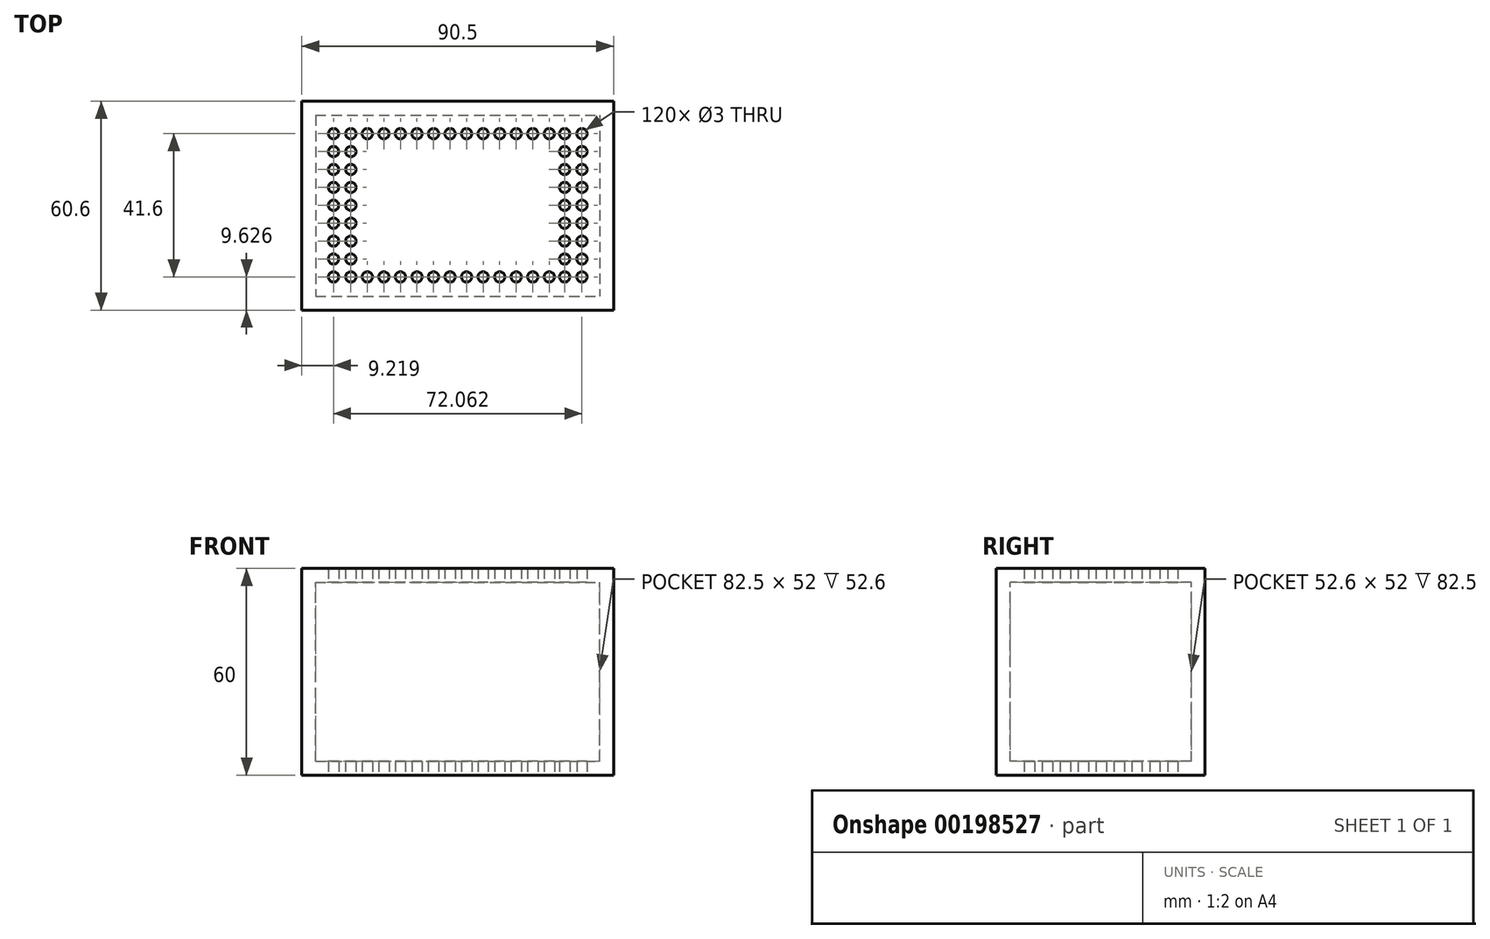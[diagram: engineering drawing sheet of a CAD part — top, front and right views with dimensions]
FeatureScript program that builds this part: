
annotation { "Feature Type Name" : "Feature", "Feature Type Description" : "" }
export const myFeature = defineFeature(function(context is Context, id is Id, definition is map)
    precondition{}
    {
        {
            var Q0;
            Q0=qCreatedBy(makeId("Top.planeOp"),FACE);
            var sketch = newSketch(context, id + "F0", { "sketchPlane" : qUnion([Q0])});
            skLineSegment(sketch, "E0.bottom", {"start": v(-45.25, 30.3) * mm, "end": v(45.25, 30.3) * mm});
            skLineSegment(sketch, "E0.top", {"start": v(-45.25, -30.3) * mm, "end": v(45.25, -30.3) * mm});
            skLineSegment(sketch, "E0.left", {"start": v(-45.25, 30.3) * mm, "end": v(-45.25, -30.3) * mm});
            skLineSegment(sketch, "E0.right", {"start": v(45.25, 30.3) * mm, "end": v(45.25, -30.3) * mm});
            skLineSegment(sketch, "E1", {"start": v(-45.25, -30.3) * mm, "end": v(45.25, 30.3) * mm, "construction": true});
            skLineSegment(sketch, "E2.0", {"start": v(41.25, 26.3) * mm, "end": v(41.25, -26.3) * mm});
            skLineSegment(sketch, "E2.1", {"start": v(-41.25, 26.3) * mm, "end": v(41.25, 26.3) * mm});
            skLineSegment(sketch, "E2.2", {"start": v(-41.25, 26.3) * mm, "end": v(-41.25, -26.3) * mm});
            skLineSegment(sketch, "E2.3", {"start": v(-41.25, -26.3) * mm, "end": v(41.25, -26.3) * mm});
            skCircle(sketch, "E3", {"center": v(-36.03, -20.67) * mm, "radius": 1.5 * mm});
            skLineSegment(sketch, "E4", {"start": v(0, -43.44) * mm, "end": v(0, 37) * mm, "construction": true});
            skPoint(sketch, "E4.endSnap0", {"position": v(0, 30.3) * mm});
            skCircle(sketch, "E5.0.1.0", {"center": v(-36.03, -15.47) * mm, "radius": 1.5 * mm});
            skCircle(sketch, "E5.0.2.0", {"center": v(-36.03, -10.27) * mm, "radius": 1.5 * mm});
            skCircle(sketch, "E5.0.3.0", {"center": v(-36.03, -5.07) * mm, "radius": 1.5 * mm});
            skCircle(sketch, "E5.0.4.0", {"center": v(-36.03, 0.13) * mm, "radius": 1.5 * mm});
            skCircle(sketch, "E5.0.5.0", {"center": v(-36.03, 5.33) * mm, "radius": 1.5 * mm});
            skCircle(sketch, "E5.0.6.0", {"center": v(-36.03, 10.53) * mm, "radius": 1.5 * mm});
            skCircle(sketch, "E5.0.7.0", {"center": v(-36.03, 15.73) * mm, "radius": 1.5 * mm});
            skCircle(sketch, "E5.0.8.0", {"center": v(-36.03, 20.93) * mm, "radius": 1.5 * mm});
            skCircle(sketch, "E5.1.0.0", {"center": v(-31.03, -20.67) * mm, "radius": 1.5 * mm});
            skCircle(sketch, "E5.1.1.0", {"center": v(-31.03, -15.47) * mm, "radius": 1.5 * mm});
            skCircle(sketch, "E5.1.2.0", {"center": v(-31.03, -10.27) * mm, "radius": 1.5 * mm});
            skCircle(sketch, "E5.1.3.0", {"center": v(-31.03, -5.07) * mm, "radius": 1.5 * mm});
            skCircle(sketch, "E5.1.4.0", {"center": v(-31.03, 0.13) * mm, "radius": 1.5 * mm});
            skCircle(sketch, "E5.1.5.0", {"center": v(-31.03, 5.33) * mm, "radius": 1.5 * mm});
            skCircle(sketch, "E5.1.6.0", {"center": v(-31.03, 10.53) * mm, "radius": 1.5 * mm});
            skCircle(sketch, "E5.1.7.0", {"center": v(-31.03, 15.73) * mm, "radius": 1.5 * mm});
            skCircle(sketch, "E5.1.8.0", {"center": v(-31.03, 20.93) * mm, "radius": 1.5 * mm});
            skLineSegment(sketch, "E5.direction1", {"start": v(-36.03, -20.67) * mm, "end": v(-31.03, -20.67) * mm, "construction": true});
            skLineSegment(sketch, "E5.direction2", {"start": v(-36.03, -20.67) * mm, "end": v(-36.03, -15.47) * mm, "construction": true});
            skCircle(sketch, "E6.MirrorC", {"center": v(36.03, 10.53) * mm, "radius": 1.5 * mm});
            skCircle(sketch, "E7.MirrorC", {"center": v(36.03, 5.33) * mm, "radius": 1.5 * mm});
            skCircle(sketch, "E8.MirrorC", {"center": v(36.03, -15.47) * mm, "radius": 1.5 * mm});
            skCircle(sketch, "E9.MirrorC", {"center": v(31.03, 20.93) * mm, "radius": 1.5 * mm});
            skCircle(sketch, "E10.MirrorC", {"center": v(36.03, 20.93) * mm, "radius": 1.5 * mm});
            skCircle(sketch, "E11.MirrorC", {"center": v(31.03, 5.33) * mm, "radius": 1.5 * mm});
            skCircle(sketch, "E12.MirrorC", {"center": v(31.03, 10.53) * mm, "radius": 1.5 * mm});
            skCircle(sketch, "E13.MirrorC", {"center": v(31.03, -20.67) * mm, "radius": 1.5 * mm});
            skLineSegment(sketch, "E14.MirrorCS", {"start": v(36.03, -20.67) * mm, "end": v(36.03, -15.47) * mm, "construction": true});
            skCircle(sketch, "E15.MirrorC", {"center": v(31.03, -10.27) * mm, "radius": 1.5 * mm});
            skCircle(sketch, "E16.MirrorC", {"center": v(31.03, 0.13) * mm, "radius": 1.5 * mm});
            skCircle(sketch, "E17.MirrorC", {"center": v(36.03, 15.73) * mm, "radius": 1.5 * mm});
            skCircle(sketch, "E18.MirrorC", {"center": v(31.03, -5.07) * mm, "radius": 1.5 * mm});
            skCircle(sketch, "E19.MirrorC", {"center": v(36.03, 0.13) * mm, "radius": 1.5 * mm});
            skLineSegment(sketch, "E20.MirrorCS", {"start": v(36.03, -20.67) * mm, "end": v(31.03, -20.67) * mm, "construction": true});
            skCircle(sketch, "E21.MirrorC", {"center": v(31.03, 15.73) * mm, "radius": 1.5 * mm});
            skCircle(sketch, "E22.MirrorC", {"center": v(31.03, -15.47) * mm, "radius": 1.5 * mm});
            skCircle(sketch, "E23.MirrorC", {"center": v(36.03, -10.27) * mm, "radius": 1.5 * mm});
            skCircle(sketch, "E24.MirrorC", {"center": v(36.03, -5.07) * mm, "radius": 1.5 * mm});
            skCircle(sketch, "E25.MirrorC", {"center": v(36.03, -20.67) * mm, "radius": 1.5 * mm});
            skCircle(sketch, "E26.1.0.0", {"center": v(-26.23, -20.67) * mm, "radius": 1.5 * mm});
            skCircle(sketch, "E26.1.0.1", {"center": v(-26.23, 20.93) * mm, "radius": 1.5 * mm});
            skCircle(sketch, "E26.2.0.0", {"center": v(-21.43, -20.67) * mm, "radius": 1.5 * mm});
            skCircle(sketch, "E26.2.0.1", {"center": v(-21.43, 20.93) * mm, "radius": 1.5 * mm});
            skCircle(sketch, "E26.3.0.0", {"center": v(-16.63, -20.67) * mm, "radius": 1.5 * mm});
            skCircle(sketch, "E26.3.0.1", {"center": v(-16.63, 20.93) * mm, "radius": 1.5 * mm});
            skCircle(sketch, "E26.4.0.0", {"center": v(-11.83, -20.67) * mm, "radius": 1.5 * mm});
            skCircle(sketch, "E26.4.0.1", {"center": v(-11.83, 20.93) * mm, "radius": 1.5 * mm});
            skCircle(sketch, "E26.5.0.0", {"center": v(-7.03, -20.67) * mm, "radius": 1.5 * mm});
            skCircle(sketch, "E26.5.0.1", {"center": v(-7.03, 20.93) * mm, "radius": 1.5 * mm});
            skCircle(sketch, "E26.6.0.0", {"center": v(-2.23, -20.67) * mm, "radius": 1.5 * mm});
            skCircle(sketch, "E26.6.0.1", {"center": v(-2.23, 20.93) * mm, "radius": 1.5 * mm});
            skCircle(sketch, "E26.7.0.0", {"center": v(2.57, -20.67) * mm, "radius": 1.5 * mm});
            skCircle(sketch, "E26.7.0.1", {"center": v(2.57, 20.93) * mm, "radius": 1.5 * mm});
            skCircle(sketch, "E26.8.0.0", {"center": v(7.37, -20.67) * mm, "radius": 1.5 * mm});
            skCircle(sketch, "E26.8.0.1", {"center": v(7.37, 20.93) * mm, "radius": 1.5 * mm});
            skCircle(sketch, "E26.9.0.0", {"center": v(12.17, -20.67) * mm, "radius": 1.5 * mm});
            skCircle(sketch, "E26.9.0.1", {"center": v(12.17, 20.93) * mm, "radius": 1.5 * mm});
            skCircle(sketch, "E26.10.0.0", {"center": v(16.97, -20.67) * mm, "radius": 1.5 * mm});
            skCircle(sketch, "E26.10.0.1", {"center": v(16.97, 20.93) * mm, "radius": 1.5 * mm});
            skCircle(sketch, "E26.11.0.0", {"center": v(21.77, -20.67) * mm, "radius": 1.5 * mm});
            skCircle(sketch, "E26.11.0.1", {"center": v(21.77, 20.93) * mm, "radius": 1.5 * mm});
            skLineSegment(sketch, "E26.direction1", {"start": v(-31.03, -20.67) * mm, "end": v(-26.23, -20.67) * mm, "construction": true});
            skCircle(sketch, "E27.0.12.0", {"center": v(26.57, -20.67) * mm, "radius": 1.5 * mm});
            skCircle(sketch, "E27.2.12.0", {"center": v(26.57, 20.93) * mm, "radius": 1.5 * mm});
            skSolve(sketch);
        }
        {
            var Q0;
            Q0=makeQuery(id+"F0.imprint","IMPRINT",FACE,{"disambiguationData":[TD([[makeQuery(id+"F0.imprint","IMPRINT",EDGE,{"derivedFrom":sQuery(id+"F0.wireOp",EDGE,"E0.bottom")}),-1.0]])]});
            var Q1;
            Q1=makeQuery(id+"F0.imprint","IMPRINT",FACE,{"disambiguationData":[TD([[makeQuery(id+"F0.imprint","IMPRINT",EDGE,{"derivedFrom":sQuery(id+"F0.wireOp",EDGE,"E2.0")}),-1.0]])]});
            extrude(context, id + "F1", {"entities" : qUnion([Q0, Q1]), "endBound" : BoundingType.SYMMETRIC, "depth" : 60 * mm});
        }
        {
            var Q0;
            Q0=makeQuery(id+"F0.imprint","IMPRINT",FACE,{"disambiguationData":[TD([[makeQuery(id+"F0.imprint","IMPRINT",EDGE,{"derivedFrom":sQuery(id+"F0.wireOp",EDGE,"E2.0")}),-1.0]])]});
            extrude(context, id + "F2", {"entities" : qUnion([Q0]), "operationType" : NewBodyOperationType.REMOVE, "endBound" : BoundingType.SYMMETRIC, "oppositeDirection" : true, "depth" : 52 * mm});
        }
    });
